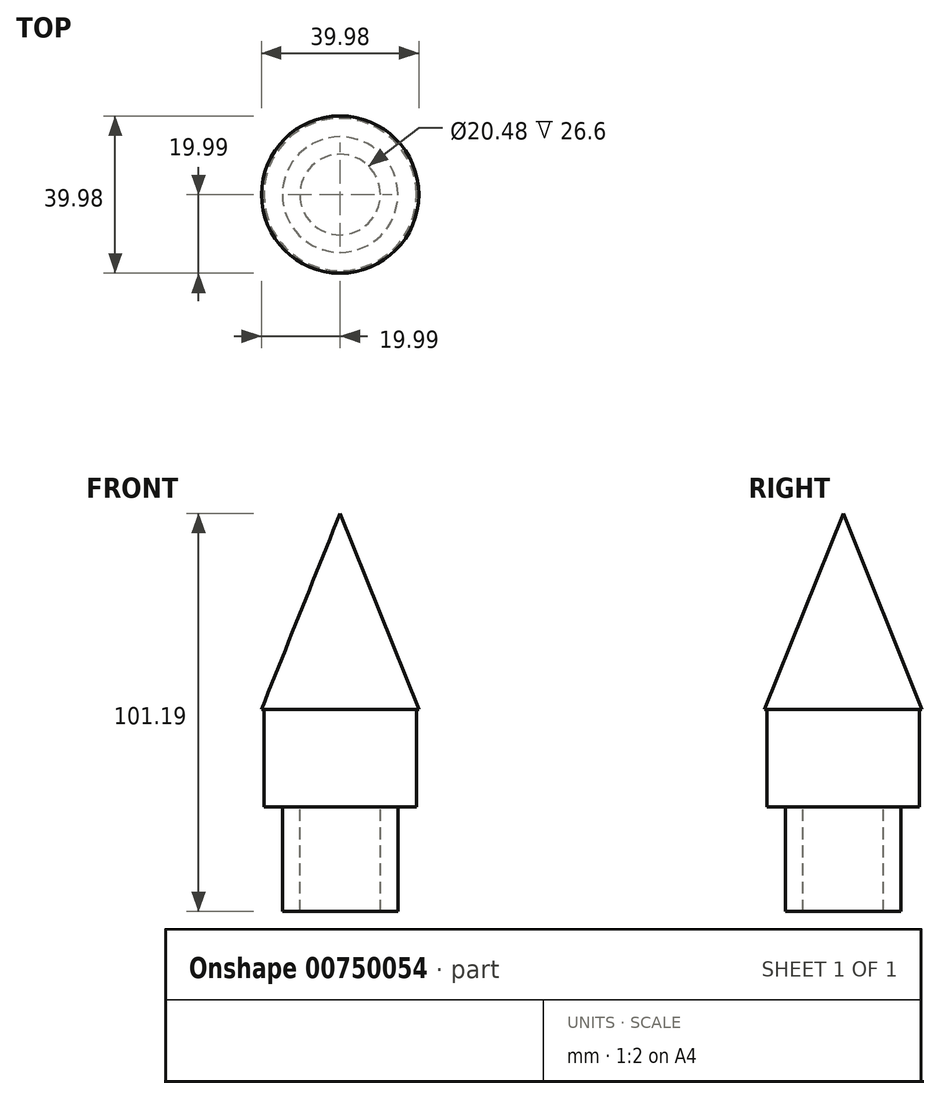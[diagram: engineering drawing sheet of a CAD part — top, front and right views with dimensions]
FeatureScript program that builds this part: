
annotation { "Feature Type Name" : "Feature", "Feature Type Description" : "" }
export const myFeature = defineFeature(function(context is Context, id is Id, definition is map)
    precondition{}
    {
        {
            var Q0;
            Q0=qCreatedBy(makeId("Top.planeOp"),FACE);
            var sketch = newSketch(context, id + "F0", { "sketchPlane" : qUnion([Q0])});
            skCircle(sketch, "E0", {"center": v(0, 0) * mm, "radius": 19.35 * mm});
            skSolve(sketch);
        }
        {
            var Q0;
            Q0 = qSketchRegion(id + "F0", true);
            extrude(context, id + "F1", {"entities" : qUnion([Q0]), "depth" : 25 * mm, "offsetDistance" : 25 * mm});
        }
        {
            var Q0;
            Q0=qCreatedBy(makeId("Right.planeOp"),FACE);
            var sketch = newSketch(context, id + "F2", { "sketchPlane" : qUnion([Q0])});
            skLineSegment(sketch, "E1", {"start": v(20, 24.77) * mm, "end": v(0, 74.6) * mm});
            skLineSegment(sketch, "E2", {"start": v(0, 74.6) * mm, "end": v(0, 24.77) * mm});
            skLineSegment(sketch, "E3", {"start": v(20, 24.77) * mm, "end": v(0, 24.77) * mm});
            skLineSegment(sketch, "E4", {"start": v(0, 0) * mm, "end": v(0, 9.82) * mm});
            skSolve(sketch);
        }
        {
            var Q0;
            Q0 = qSketchRegion(id + "F2", true);
            var Q1;
            Q1=sQuery(id+"F2.wireOp",EDGE,"E4");
            revolve(context, id + "F3", {"operationType" : NewBodyOperationType.ADD, "surfaceOperationType" : NewSurfaceOperationType.NEW, "entities" : qUnion([Q0]), "axis" : qUnion([Q1]), "revolveType" : RevolveType.FULL});
        }
        {
            var Q0;
            Q0=qCreatedBy(makeId("Top.planeOp"),FACE);
            var sketch = newSketch(context, id + "F4", { "sketchPlane" : qUnion([Q0])});
            skCircle(sketch, "E5", {"center": v(0, 0) * mm, "radius": 19.16 * mm});
            skCircle(sketch, "E6", {"center": v(0, 0) * mm, "radius": 14.67 * mm});
            skCircle(sketch, "E7", {"center": v(0, 0) * mm, "radius": 10.24 * mm});
            skSolve(sketch);
        }
        {
            var Q0;
            Q0=makeQuery(id+"F4.imprint","IMPRINT",FACE,{"disambiguationData":[TD([[makeQuery(id+"F4.imprint","IMPRINT",EDGE,{"derivedFrom":sQuery(id+"F4.wireOp",EDGE,"E6")}),1.0]])]});
            extrude(context, id + "F5", {"entities" : qUnion([Q0]), "operationType" : NewBodyOperationType.ADD, "oppositeDirection" : true, "depth" : 26.6 * mm, "offsetDistance" : 25 * mm});
        }
    });
